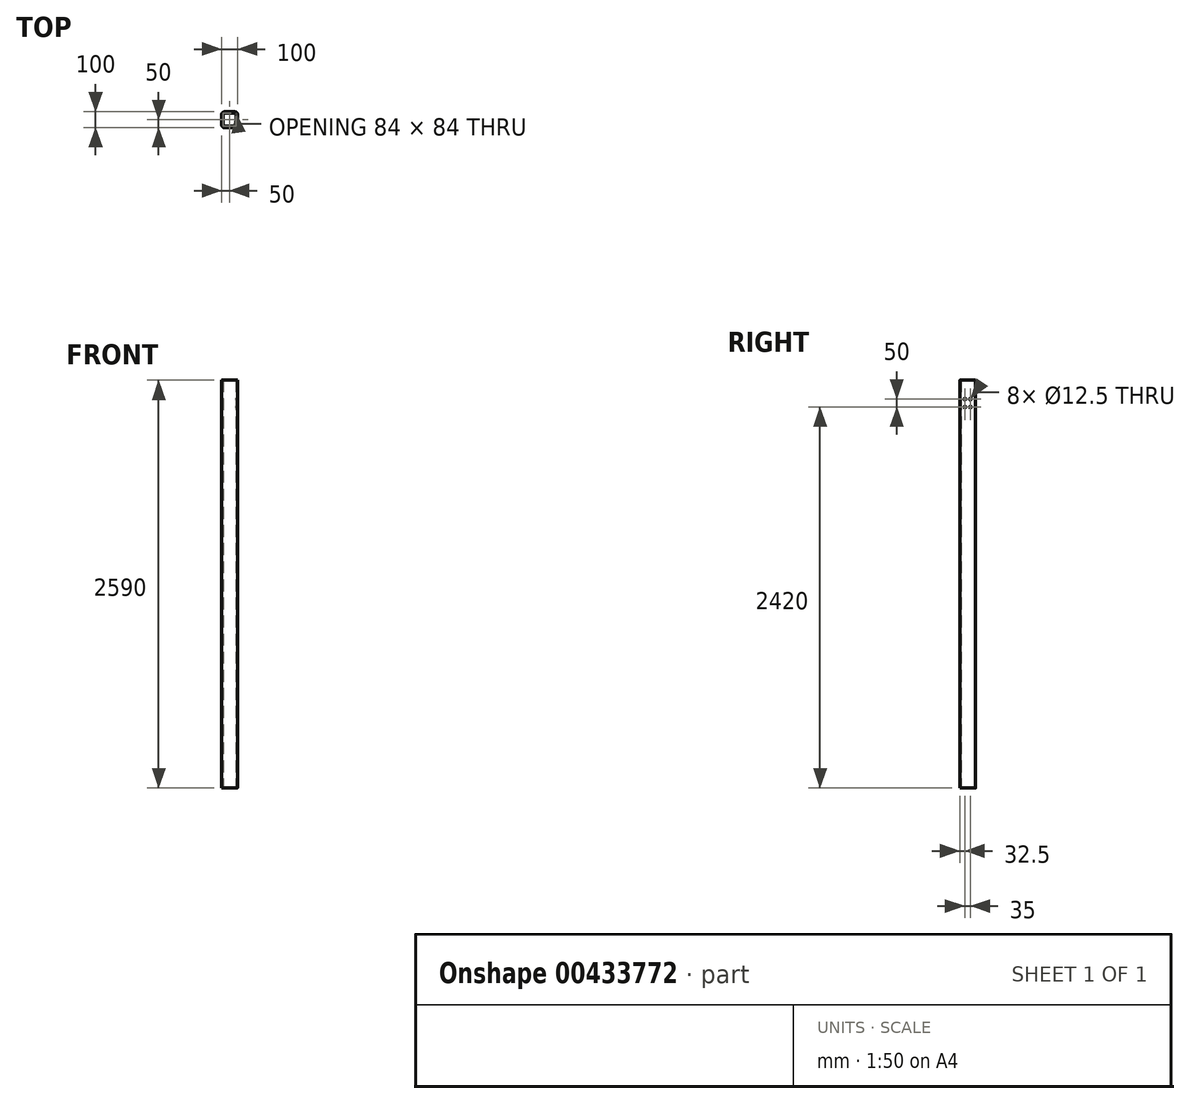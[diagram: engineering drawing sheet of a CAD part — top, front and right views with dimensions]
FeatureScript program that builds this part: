
annotation { "Feature Type Name" : "Feature", "Feature Type Description" : "" }
export const myFeature = defineFeature(function(context is Context, id is Id, definition is map)
    precondition{}
    {
        {
            var Q0;
            Q0=qCreatedBy(makeId("Top.planeOp"),FACE);
            var sketch = newSketch(context, id + "F0", { "sketchPlane" : qUnion([Q0])});
            skLineSegment(sketch, "E0.bottom", {"start": v(34, 50) * mm, "end": v(-34, 50) * mm});
            skLineSegment(sketch, "E0.top", {"start": v(34, -50) * mm, "end": v(-34, -50) * mm});
            skLineSegment(sketch, "E0.left", {"start": v(50, 34) * mm, "end": v(50, -34) * mm});
            skLineSegment(sketch, "E0.right", {"start": v(-50, 34) * mm, "end": v(-50, -34) * mm});
            skPoint(sketch, "E0.middle", {"position": v(0, 0) * mm});
            skPoint(sketch, "E1.visualSharp", {"position": v(-50, 50) * mm});
            skArc(sketch, "E1.filletArc", {"start": v(-34, 50) * mm, "mid": v(-45.31, 45.31) * mm, "end": v(-50, 34) * mm});
            skPoint(sketch, "E2.visualSharp", {"position": v(50, 50) * mm});
            skArc(sketch, "E2.filletArc", {"start": v(50, 34) * mm, "mid": v(45.31, 45.31) * mm, "end": v(34, 50) * mm});
            skPoint(sketch, "E3.visualSharp", {"position": v(50, -50) * mm});
            skArc(sketch, "E3.filletArc", {"start": v(34, -50) * mm, "mid": v(45.31, -45.31) * mm, "end": v(50, -34) * mm});
            skPoint(sketch, "E4.visualSharp", {"position": v(-50, -50) * mm});
            skArc(sketch, "E4.filletArc", {"start": v(-50, -34) * mm, "mid": v(-45.31, -45.31) * mm, "end": v(-34, -50) * mm});
            skArc(sketch, "E5.0", {"start": v(42, 34) * mm, "mid": v(39.66, 39.66) * mm, "end": v(34, 42) * mm});
            skLineSegment(sketch, "E5.1", {"start": v(42, 34) * mm, "end": v(42, -34) * mm});
            skLineSegment(sketch, "E5.2", {"start": v(34, 42) * mm, "end": v(-34, 42) * mm});
            skArc(sketch, "E5.3", {"start": v(34, -42) * mm, "mid": v(39.66, -39.66) * mm, "end": v(42, -34) * mm});
            skArc(sketch, "E5.4", {"start": v(-34, 42) * mm, "mid": v(-39.66, 39.66) * mm, "end": v(-42, 34) * mm});
            skLineSegment(sketch, "E5.5", {"start": v(-42, 34) * mm, "end": v(-42, -34) * mm});
            skArc(sketch, "E5.6", {"start": v(-42, -34) * mm, "mid": v(-39.66, -39.66) * mm, "end": v(-34, -42) * mm});
            skLineSegment(sketch, "E5.7", {"start": v(34, -42) * mm, "end": v(-34, -42) * mm});
            skSolve(sketch);
        }
        {
            var Q0;
            Q0 = qSketchRegion(id + "F0", true);
            extrude(context, id + "F1", {"entities" : qUnion([Q0]), "depth" : 2590 * mm});
        }
        {
            var Q0;
            Q0=makeQuery(id+"F1.opExtrude","SWEPT_FACE",FACE,{"disambiguationData":[OSD([sQuery(id+"F0.wireOp",EDGE,"E0.left")])]});
            var sketch = newSketch(context, id + "F2", { "sketchPlane" : qUnion([Q0])});
            skLineSegment(sketch, "E6", {"start": v(34, 2490) * mm, "end": v(-34, 2490) * mm, "construction": true});
            skLineSegment(sketch, "E7", {"start": v(0, 2490) * mm, "end": v(0, 2420) * mm, "construction": true});
            skCircle(sketch, "E8", {"center": v(-17.5, 2470) * mm, "radius": 6.25 * mm});
            skCircle(sketch, "E9.0.1.0", {"center": v(-17.5, 2420) * mm, "radius": 6.25 * mm});
            skLineSegment(sketch, "E9.direction1", {"start": v(-17.5, 2470) * mm, "end": v(0, 2470) * mm, "construction": true});
            skLineSegment(sketch, "E9.direction2", {"start": v(-17.5, 2470) * mm, "end": v(-17.5, 2420) * mm, "construction": true});
            skCircle(sketch, "E10.MirrorC", {"center": v(17.5, 2420) * mm, "radius": 6.25 * mm});
            skCircle(sketch, "E11.MirrorC", {"center": v(17.5, 2470) * mm, "radius": 6.25 * mm});
            skSolve(sketch);
        }
        {
            var Q0;
            Q0 = qSketchRegion(id + "F2", true);
            extrude(context, id + "F3", {"entities" : qUnion([Q0]), "operationType" : NewBodyOperationType.REMOVE, "endBound" : BoundingType.THROUGH_ALL, "oppositeDirection" : true, "depth" : 25 * mm});
        }
    });
